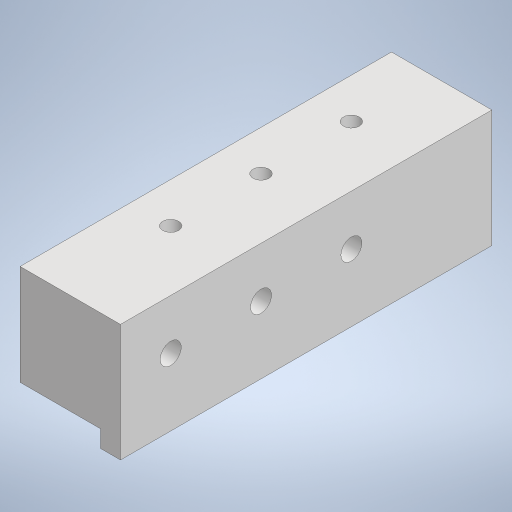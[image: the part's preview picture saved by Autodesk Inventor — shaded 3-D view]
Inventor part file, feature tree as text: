
AUTODESK INVENTOR PART (.ipt)
format: ipt  version: 2024.1 (Build 281209000, 209)  size: 290,816 bytes
history: native  units: in
note: dims shown in document units (in); Inventor stores cm internally (conversion verified against a paired STEP export)
features: extrude x7, sketch x7, chamfer x1, mirror x1
ambient origin geometry x8: Origin, YZ Plane, XZ Plane, XY Plane, X Axis, Y Axis, Z Axis, Center Point
bodies: Solid1 (feature_tree)
feature tree (16):
  extrude  "Extrusion1"  Depth=0.3937in
  extrude  "Extrusion2"  Depth=0.0787in
  extrude  "Extrusion3"  Depth=0.0669in
  extrude  "Extrusion4"  Depth=0.315in
  extrude  "Extrusion5"  Depth=0.1575in
  chamfer  "Chamfer1"  [1 undecoded]
  extrude  "Extrusion6"  Depth=0.315in
  extrude  "Extrusion7"  Depth=0.315in
  mirror  "Mirror1"
  sketch  "Sketch1"  dims[d0=1.1024in d1=0.3937in]
  sketch  "Sketch2"  dims[d2=0.3937in d3=0.0in d4=0.0787in]
  sketch  "Sketch3"  dims[d5=0.0669in d6=0.0in d7=0.063in]
  sketch  "Sketch4"  dims[d8=0.063in d9=0.315in]
  sketch  "Sketch5"  dims[d10=0.3543in d11=0.1575in]
  sketch  "Sketch6"  dims[d12=0.1575in d13=0.0in d14=0.0in]
  sketch  "Sketch7"  dims[d15=0.0827in d16=0.0827in d17=0.0827in d18=0.1969in d19=0.1969in d20=0.1969in d21=0.1969in d22=0.3543in d23=0.3543in d24=0.0in d25=0.0in d26=0.1575in d27=0.1575in d28=0.1575in d29=0.0984in d30=0.0in d31=0.0354in d32=0.0787in d33=45.0deg d34=0.3543in d35=0.0in d39=0.063in d40=0.1575in d41=0.315in d42=0.0in d43=0.0in]
note: 1 required parameter value undecoded (feature->parameter linkage not recoverable at this tier; creation-order binding heuristic only, values carry confidence <= 0.55)
